# Revit family: ASSA_ABLOY_Security_MP100_WallHosted
name_source: partatom
category: Doors
units: mm (PartAtom-declared; Revit-internal decimal feet)

## family parameters
Always vertical = Yes
Cut with Voids When Loaded = No
Host = Wall
Room Calculation Point = No
Shared = No

## types (6) — shared parameters
AccessibilityPerformance = 4-6/min.
AccessoryOptions = contact manufacturer
AntiFingerTrapRequirement = No
Assembly Code = B2030300
Capacity = 4-6/min.
Category = Security gate/portal
Colour = Aluminium
Construction Type = Automatic Revolving Door
Description = Circular sliding door
DoorNumber = 2
DoorsetOperation = automatic
DrumWallPanelFill = ASSA ABLOY Laminated Safety Glass (Clear)
DurationUnit = Year
ElectronicLock = Yes
Features = Separation, anti-tailgating, anti-piggybacking
Finish = Powder coated, Anodized, customer specific
FireExit = No
Flooring = ASSA ABLOY Felt Carpet
FrameFinishOptions = Stainless steel and more
FrameMaterial = Aluminium
FrameProfile = Aluminium
FrameSeal = Yes
Function = Exterior
GlassLayers = 2
GlassThickness1 = 8
GlassThickness2 = 10
GlassType = part of glazing spec
HasDrive = Yes
IfcExportAs = IFCDoorStyle
IfcExportType = Door
IsExternal = Yes
IssueDate = <>
LeafColourOptions = all RAL, customer specific
LeafPanelFill = ASSA ABLOY Laminated Safety Glass
Manufacturer = ASSA ABLOY
ManufacturerName = ASSA ABLOY
ManufacturerURL = www.assaabloyentrance.com
Material = Aluminium
Model = MP 100
ModelReference = depends on the configuration
NBSDescription = Sliding Doorset
NBSReference = 25-50-20/175
NominalHeight = 640080 mm
OpenEntry = No
OpenExit = No
Operation = automatic
PanelFrames = ASSA ABLOY Aluminium
ReferenceStandard = EN16005, EN16361, DIN 18650, etc.
ReplacementCost = Depends on the configuration and door type
SafetyDevices = Optical sensors
SelfClosing = Yes
ServiceLifeDuration = 10-15 years
Shape = Cylinder Shaped
Size = XxxXXxXX
SmokeStop = No
ThresholdRequired = No
URL = www.assaabloyentrance.com
Uniclass2 = Ss_25_30_20_77
Version = 1
WarrantyDescription = Depends on country
WarrantyDurationLabour = Depends on country
WarrantyDurationParts = Depends on country
WarrantyDurationUnit = Depends on country
WarrantyGuarantorLabour = Local door manufacturer
WarrantyGuarantorParts = Local door manufacturer
WithinStandardSizes = Yes
zero-valued in all types: Cost, GlazingAreaFraction, OffsetFromWallSide, OffsetFromWallTop, ThermalTransmittance, Thickness

## per-type parameters (varying)
| type | CanopyHeight | CanopyRadius | DiameterOptions | HandicapAccessible | Height | InsideDiameter | NominalLength | NominalWidth | OuterRadius | OutsideDiameter | PassageHeight | PassageWidth | PassageWidthOptions | RecessHeight | RecessWidth | Rough Height | Rough Width | TotalDiameter | TotalHeight | WallCutHeight | Weight | Width |
| 600 mm - Double | 220 mm  [stored 0.721785 ft] | 548 mm  [stored 1.7979 ft] | 1035mm, 1090mm depends on glas type | No | 2420 mm | 967 mm | 315468 mm | 315468 mm | 545 mm  [stored 1.78806 ft] | 1090 mm  [stored 3.57612 ft] | 2200 mm | 469.1 mm  [stored 1.53904 ft] | 600 | 2470 mm | 1298.2 mm  [stored 4.25919 ft] | 2426 mm | 1252.3 mm | 1198.2 mm  [stored 3.9311 ft] | 2420 mm | 2475 mm | ca. 355-475kg | 1115 mm  [stored 3.65814 ft] |
| 900 mm - Double | 610 mm  [stored 2.00131 ft] | 758 mm  [stored 2.48688 ft] | 1455mm, 1510mm depends on glas type | Yes | 3210 mm | 1387 mm  [stored 4.55052 ft] | 443484 mm | 443484 mm | 755 mm  [stored 2.47703 ft] | 1510 mm  [stored 4.95407 ft] | 2600 mm | 679.1 mm  [stored 2.22802 ft] | 900 | 3260 mm | 1718.2 mm | 3216 mm | 1672.3 mm | 1618.2 mm | 3210 mm | 3265 mm | ca. 460-640kg | 1535 mm  [stored 5.03609 ft] |
| 1100 mm - Double | 1000 mm  [stored 3.28084 ft] | 898 mm  [stored 2.94619 ft] | 1735mm, 1790mm depends on glas type | Yes | 4000 mm | 1667 mm | 528828 mm | 528828 mm | 895 mm  [stored 2.93635 ft] | 1790 mm | 3000 mm | 819.1 mm  [stored 2.68734 ft] | 1100 | 4050 mm | 1998.2 mm | 4006 mm | 1952.3 mm | 1898.2 mm | 4000 mm | 4055 mm | ca. 538-760kg | 1815 mm |
| 1100 mm - Single | 1000 mm  [stored 3.28084 ft] | 870.5 mm  [stored 2.85597 ft] | 1735mm, 1790mm depends on glas type | Yes | 4000 mm | 1612 mm | 528828 mm | 528828 mm | 867.5 mm  [stored 2.84613 ft] | 1735 mm | 3000 mm | 791.6 mm  [stored 2.59711 ft] | 1100 | 4050 mm | 1943.2 mm | 4006 mm | 1897.3 mm | 1843.2 mm | 4000 mm | 4055 mm | ca. 538-760kg | 1760 mm |
| 900 mm - Single | 610 mm  [stored 2.00131 ft] | 730.5 mm  [stored 2.39665 ft] | 1455mm, 1510mm depends on glas type | Yes | 3210 mm | 1332 mm  [stored 4.37008 ft] | 443484 mm | 443484 mm | 727.5 mm  [stored 2.38681 ft] | 1455 mm  [stored 4.77362 ft] | 2600 mm | 651.6 mm  [stored 2.1378 ft] | 900 | 3260 mm | 1663.2 mm | 3216 mm | 1617.3 mm | 1563.2 mm | 3210 mm | 3265 mm | ca. 460-640kg | 1480 mm  [stored 4.85564 ft] |
| 600 mm - Single | 220 mm  [stored 0.721785 ft] | 520.5 mm | 1035mm, 1090mm depends on glas type | No | 2420 mm | 912 mm | 315468 mm | 315468 mm | 517.5 mm | 1035 mm  [stored 3.39567 ft] | 2200 mm | 441.6 mm  [stored 1.44882 ft] | 600 | 2470 mm | 1243.2 mm  [stored 4.07874 ft] | 2426 mm | 1197.3 mm | 1143.2 mm | 2420 mm | 2475 mm | ca. 355-475kg | 1060 mm |

note: [stored X ft] marks values corroborated as IEEE doubles in the binary element streams (Revit-internal decimal feet)

## geometry (parser evidence)
native form markers: Blend x16, Sweep x7
no freeform markers — native parametric forms only
